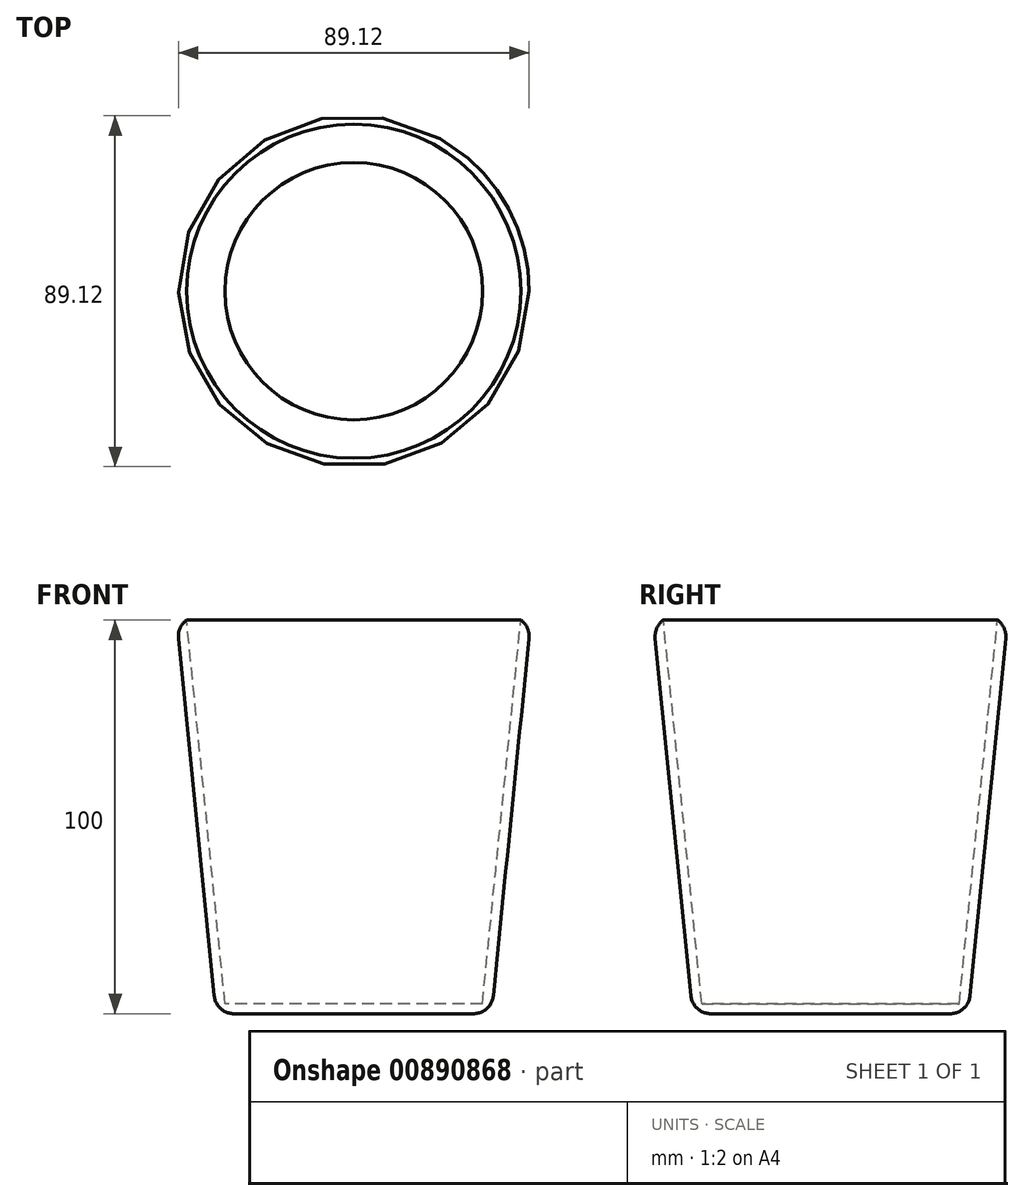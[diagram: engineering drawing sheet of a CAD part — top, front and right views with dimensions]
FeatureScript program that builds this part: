
annotation { "Feature Type Name" : "Feature", "Feature Type Description" : "" }
export const myFeature = defineFeature(function(context is Context, id is Id, definition is map)
    precondition{}
    {
        {
            var Q0;
            Q0=qCreatedBy(makeId("Front.planeOp"),FACE);
            var sketch = newSketch(context, id + "F0", { "sketchPlane" : qUnion([Q0])});
            skLineSegment(sketch, "E0", {"start": v(-5.38, 43.79) * mm, "end": v(-5.38, -56.21) * mm});
            skLineSegment(sketch, "E1", {"start": v(-5.38, -56.21) * mm, "end": v(29.62, -56.21) * mm});
            skLineSegment(sketch, "E2", {"start": v(-5.38, 43.79) * mm, "end": v(39.62, 43.79) * mm});
            skLineSegment(sketch, "E3", {"start": v(39.62, 43.79) * mm, "end": v(29.62, -56.21) * mm});
            skFitSpline(sketch, "E4", {"points": [v(38.32, 30.72) * mm, v(72.52, 11.45) * mm, v(71.32, -31.2) * mm, v(30.63, -46.16) * mm], "startDerivative": vector(126.83, -36.76) * mm, "endDerivative": vector(-143.45, -17.3) * mm});
            skSolve(sketch);
        }
        {
            var Q0;
            Q0=makeQuery(id+"F0.imprint","IMPRINT",FACE,{"disambiguationData":[TD([[makeQuery(id+"F0.imprint","IMPRINT",EDGE,{"derivedFrom":sQuery(id+"F0.wireOp",EDGE,"E0")}),1.0]])]});
            var Q1;
            Q1=sQuery(id+"F0.wireOp",EDGE,"E0");
            revolve(context, id + "F1", {"surfaceOperationType" : NewSurfaceOperationType.NEW, "entities" : qUnion([Q0]), "axis" : qUnion([Q1]), "revolveType" : RevolveType.FULL});
        }
        {
            var Q0;
            Q0=makeQuery(id+"F1.opRevolve","SWEPT_FACE",FACE,{"disambiguationData":[OSD([sQuery(id+"F0.wireOp",EDGE,"E2")])]});
            shell(context, id + "F2", {"entities" : qUnion([Q0]), "thickness" : 2.54 * mm});
        }
        {
            var Q0;
            Q0=makeQuery(id+"F1.opRevolve","SWEPT_EDGE",EDGE,{"disambiguationData":[OSD([sQuery(id+"F0.wireOp",EDGE,"E1"),sQuery(id+"F0.wireOp",EDGE,"E3")])]});
            var Q1;
            Q1=makeQuery(id+"F1.opRevolve","SWEPT_FACE",FACE,{"disambiguationData":[OSD([sQuery(id+"F0.wireOp",EDGE,"E3")])]});
            fillet(context, id + "F3", {"entities" : qUnion([Q0, Q1]), "radius" : 5.08 * mm, "tangentPropagation" : true, "allowEdgeOverflow" : false});
        }
        {
            var Q0;
            Q0=sQuery(id+"F0.wireOp",EDGE,"8a2f8c94-dc14-4f7a-a346-cce47c6c2b46.0");
            var Q1;
            Q1=sQuery(id+"F0.wireOp",EDGE,"E4");
            extrude(context, id + "F4", {"bodyType" : ToolBodyType.SURFACE, "surfaceEntities" : qUnion([Q0, Q1]), "endBound" : BoundingType.SYMMETRIC, "depth" : 10 * mm, "offsetDistance" : 25.4 * mm});
        }
    });
